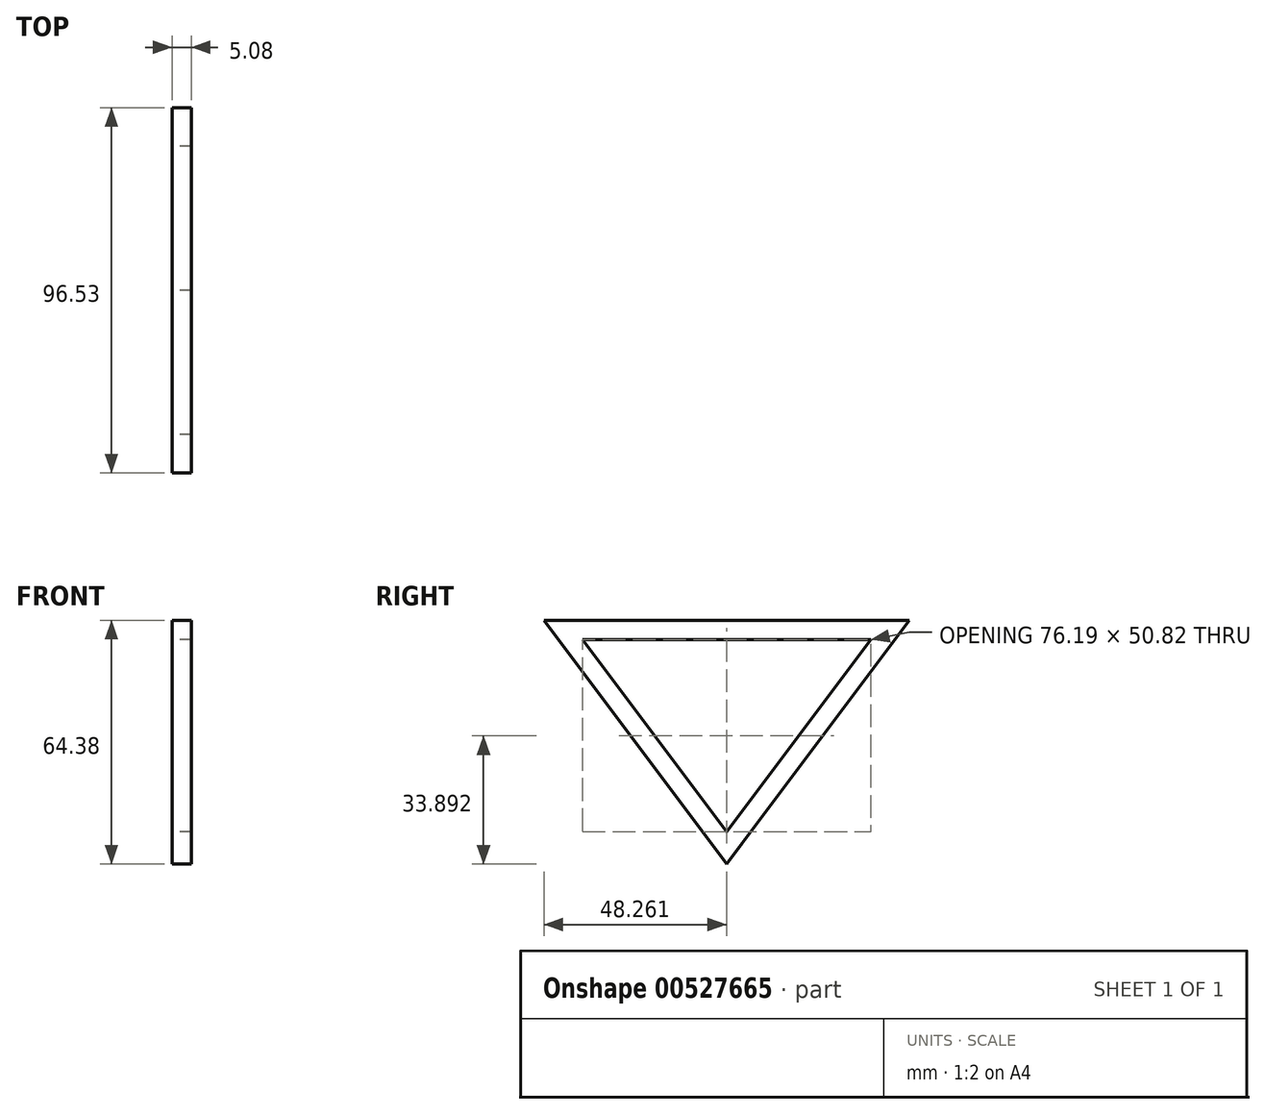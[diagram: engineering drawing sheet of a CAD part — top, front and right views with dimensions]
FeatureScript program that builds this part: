
annotation { "Feature Type Name" : "Feature", "Feature Type Description" : "" }
export const myFeature = defineFeature(function(context is Context, id is Id, definition is map)
    precondition{}
    {
        {
            var Q0;
            Q0=qCreatedBy(makeId("Right.planeOp"),FACE);
            var sketch = newSketch(context, id + "F0", { "sketchPlane" : qUnion([Q0])});
            skLineSegment(sketch, "E0.bottom", {"start": v(-35.57, 22.06) * mm, "end": v(40.62, 22.06) * mm});
            skPoint(sketch, "E1.oppositeSnap0", {"position": v(2.52, 19.65) * mm});
            skLineSegment(sketch, "E1.bottom", {"start": v(-35.57, 22.06) * mm, "end": v(2.52, 22.06) * mm});
            skLineSegment(sketch, "E2", {"start": v(-35.57, 22.06) * mm, "end": v(2.52, -28.76) * mm});
            skLineSegment(sketch, "E3", {"start": v(2.52, -28.76) * mm, "end": v(40.62, 22.06) * mm});
            skLineSegment(sketch, "E4.top", {"start": v(-35.57, 27.14) * mm, "end": v(40.62, 27.14) * mm});
            skLineSegment(sketch, "E4.left", {"start": v(-35.57, 22.06) * mm, "end": v(-35.57, 27.14) * mm});
            skLineSegment(sketch, "E4.right", {"start": v(40.62, 22.06) * mm, "end": v(40.62, 27.14) * mm});
            skLineSegment(sketch, "E5", {"start": v(-35.57, 22.06) * mm, "end": v(-39.64, 19) * mm});
            skLineSegment(sketch, "E6", {"start": v(2.52, -28.76) * mm, "end": v(-1.55, -31.8) * mm});
            skLineSegment(sketch, "E7", {"start": v(-1.55, -31.8) * mm, "end": v(-39.64, 19) * mm});
            skLineSegment(sketch, "E8", {"start": v(2.52, -28.76) * mm, "end": v(6.59, -31.8) * mm});
            skLineSegment(sketch, "E9", {"start": v(40.62, 22.06) * mm, "end": v(44.69, 19) * mm});
            skLineSegment(sketch, "E10", {"start": v(44.69, 19) * mm, "end": v(6.59, -31.8) * mm});
            skPoint(sketch, "E11", {"position": v(2.52, -37.24) * mm});
            skPoint(sketch, "E12", {"position": v(44.69, 19) * mm});
            skPoint(sketch, "E13", {"position": v(-39.64, 19) * mm});
            skLineSegment(sketch, "E14", {"start": v(6.59, -31.8) * mm, "end": v(2.52, -37.24) * mm});
            skLineSegment(sketch, "E15", {"start": v(-1.55, -31.8) * mm, "end": v(2.52, -37.24) * mm});
            skPoint(sketch, "E16", {"position": v(50.79, 27.14) * mm});
            skLineSegment(sketch, "E17", {"start": v(40.62, 27.14) * mm, "end": v(50.79, 27.14) * mm});
            skLineSegment(sketch, "E18", {"start": v(50.79, 27.14) * mm, "end": v(44.69, 19) * mm});
            skPoint(sketch, "E19", {"position": v(-45.74, 27.14) * mm});
            skLineSegment(sketch, "E20", {"start": v(-35.57, 27.14) * mm, "end": v(-45.74, 27.14) * mm});
            skLineSegment(sketch, "E21", {"start": v(-39.64, 19) * mm, "end": v(-45.74, 27.14) * mm});
            skSolve(sketch);
        }
        {
            var Q0;
            Q0 = qSketchRegion(id + "F0", true);
            extrude(context, id + "F1", {"entities" : qUnion([Q0]), "depth" : 5.08 * mm, "offsetDistance" : 25.4 * mm});
        }
    });
